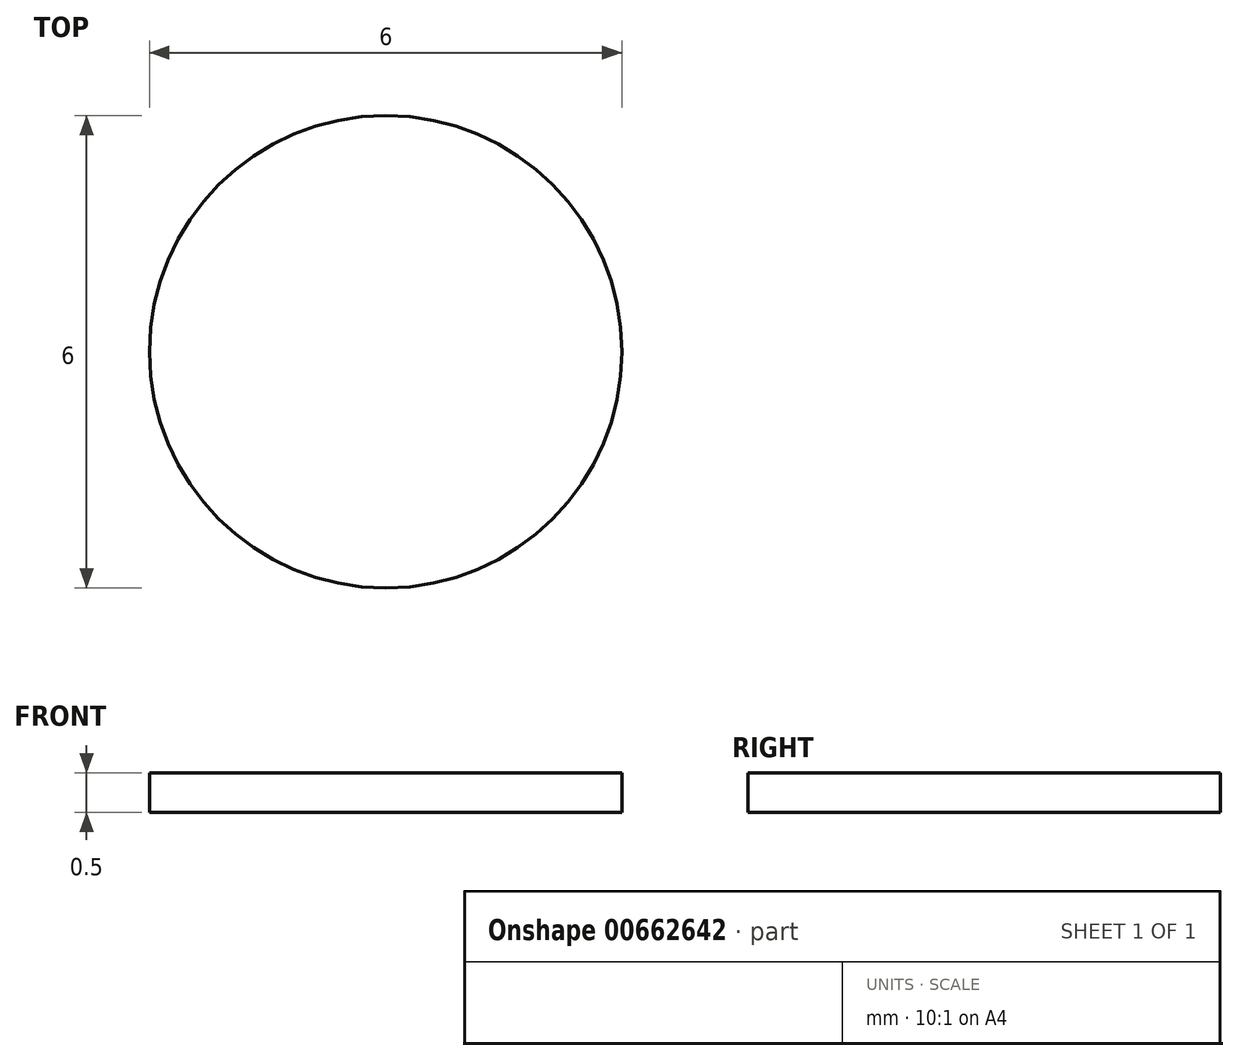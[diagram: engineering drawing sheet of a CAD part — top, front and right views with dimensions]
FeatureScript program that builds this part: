
annotation { "Feature Type Name" : "Feature", "Feature Type Description" : "" }
export const myFeature = defineFeature(function(context is Context, id is Id, definition is map)
    precondition{}
    {
        {
            var Q0;
            Q0=qCreatedBy(makeId("Top.planeOp"),FACE);
            var sketch = newSketch(context, id + "F0", { "sketchPlane" : qUnion([Q0])});
            skCircle(sketch, "E0", {"center": v(0, 0) * mm, "radius": 3 * mm});
            skSolve(sketch);
        }
        {
            var Q0;
            Q0=makeQuery(id+"F0.imprint","IMPRINT",FACE,{"disambiguationData":[TD([[makeQuery(id+"F0.imprint","IMPRINT",EDGE,{"derivedFrom":sQuery(id+"F0.wireOp",EDGE,"E0")}),1.0]])]});
            extrude(context, id + "F1", {"entities" : qUnion([Q0]), "depth" : .5 * mm, "offsetDistance" : 25 * mm});
        }
    });
